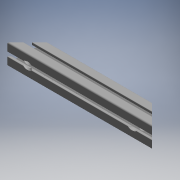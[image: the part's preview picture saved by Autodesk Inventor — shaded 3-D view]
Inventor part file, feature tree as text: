
AUTODESK INVENTOR PART (.ipt)
format: ipt  version: 2017.3 (Build 213256000, 256)  size: 354,304 bytes
history: native  units: mm (DEFAULTED — no unit token found)
features: other x56, extrude x2, revolve x2
ambient origin geometry x8: Origin, YZ Plane, XZ Plane, XY Plane, X Axis, Y Axis, Z Axis, Center Point
bodies: Solid1 (feature_tree)
feature tree (60):
  extrude  "Extrusion1"  Depth=353.553391mm TaperAngle=0.0deg
  extrude  "Extrusion2"  Depth=150.0mm TaperAngle=0.0deg
  revolve  "Revolution1"  Angle=360.0deg
  revolve  "Revolution2"  Angle=360.0deg
  other  "to_bolt21_XY"
  other  "to_bolt21_YZ"
  other  "to_bolt21_ZX"
  other  "to_bolt21_X"
  other  "to_bolt21_Y"
  other  "to_bolt21_Z"
  other  "to_bolt21_Center"
  other  "to_bolt22_XY"
  other  "to_bolt22_YZ"
  other  "to_bolt22_ZX"
  other  "to_bolt22_X"
  other  "to_bolt22_Y"
  other  "to_bolt22_Z"
  other  "to_bolt22_Center"
  other  "to_bolt23_XY"
  other  "to_bolt23_YZ"
  other  "to_bolt23_ZX"
  other  "to_bolt23_X"
  other  "to_bolt23_Y"
  other  "to_bolt23_Z"
  other  "to_bolt23_Center"
  other  "to_bolt24_XY"
  other  "to_bolt24_YZ"
  other  "to_bolt24_ZX"
  other  "to_bolt24_X"
  other  "to_bolt24_Y"
  other  "to_bolt24_Z"
  other  "to_bolt24_Center"
  other  "to_nut21_XY"
  other  "to_nut21_YZ"
  other  "to_nut21_ZX"
  other  "to_nut21_X"
  other  "to_nut21_Y"
  other  "to_nut21_Z"
  other  "to_nut21_Center"
  other  "to_nut22_XY"
  other  "to_nut22_YZ"
  other  "to_nut22_ZX"
  other  "to_nut22_X"
  other  "to_nut22_Y"
  other  "to_nut22_Z"
  other  "to_nut22_Center"
  other  "to_nut23_XY"
  other  "to_nut23_YZ"
  other  "to_nut23_ZX"
  other  "to_nut23_X"
  other  "to_nut23_Y"
  other  "to_nut23_Z"
  other  "to_nut23_Center"
  other  "to_nut24_XY"
  other  "to_nut24_YZ"
  other  "to_nut24_ZX"
  other  "to_nut24_X"
  other  "to_nut24_Y"
  other  "to_nut24_Z"
  other  "to_nut24_Center"
